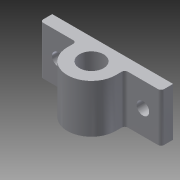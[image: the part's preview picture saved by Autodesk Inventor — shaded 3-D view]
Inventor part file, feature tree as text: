
AUTODESK INVENTOR PART (.ipt)
format: ipt  version: 2013 (Build 170138000, 138)  size: 127,488 bytes
history: native  units: in
note: dims shown in document units (in); Inventor stores cm internally (conversion verified against a paired STEP export)
features: sketch x2, extrude x2, projected_geometry x2, fillet x1
ambient origin geometry x8: Origin, YZ Plane, XZ Plane, XY Plane, X Axis, Y Axis, Z Axis, Center Point
bodies: Solid1 (feature_tree)
feature tree (7):
  sketch  "Sketch1"  dims[d0=1.0in d1=0.9375in d2=0.5in]
  extrude  "Extrusion1"  Depth=0.9375in
  fillet  "Fillet1"  Radius=0.5in
  extrude  "Extrusion3"  Depth=0.25in
  sketch  "Sketch2"  dims[d3=1.0in d4=0.0in d9=0.25in d10=0.75in d11=0.75in d12=0.25in d13=0.5in d14=0.0625in d15=0.26in d16=0.26in d17=0.25in d18=0.0in d20=0.4375in d21=1.75in]
  projected_geometry  "Projected Loop1"
  projected_geometry  "Projected Loop2"
